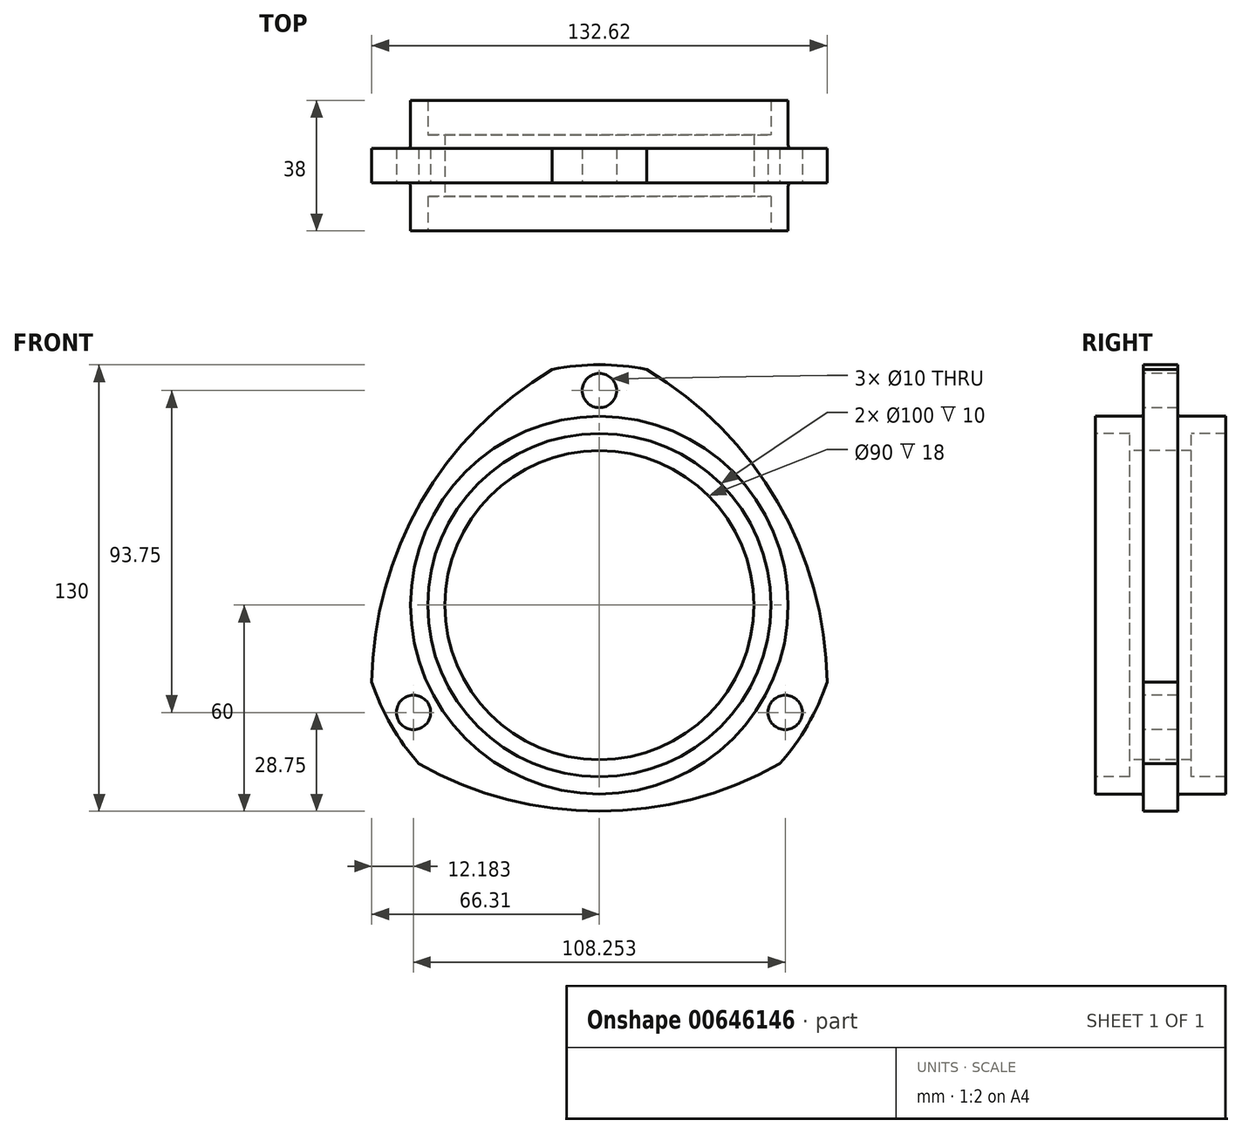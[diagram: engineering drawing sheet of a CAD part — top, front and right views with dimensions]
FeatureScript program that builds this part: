
annotation { "Feature Type Name" : "Feature", "Feature Type Description" : "" }
export const myFeature = defineFeature(function(context is Context, id is Id, definition is map)
    precondition{}
    {
        {
            var Q0;
            Q0=qCreatedBy(makeId("Right.planeOp"),FACE);
            var sketch = newSketch(context, id + "F0", { "sketchPlane" : qUnion([Q0])});
            skLineSegment(sketch, "E0", {"start": v(-36.67, 0) * mm, "end": v(37.6, 0) * mm, "construction": true});
            skLineSegment(sketch, "E1", {"start": v(0, 0) * mm, "end": v(0, 45) * mm, "construction": true});
            skLineSegment(sketch, "E2", {"start": v(-19, 50) * mm, "end": v(-9, 50) * mm});
            skLineSegment(sketch, "E3", {"start": v(-9, 50) * mm, "end": v(-9, 45) * mm});
            skLineSegment(sketch, "E4", {"start": v(-9, 45) * mm, "end": v(9, 45) * mm});
            skLineSegment(sketch, "E5", {"start": v(9, 45) * mm, "end": v(9, 50) * mm});
            skLineSegment(sketch, "E6", {"start": v(9, 50) * mm, "end": v(19, 50) * mm});
            skLineSegment(sketch, "E7", {"start": v(-19, 50) * mm, "end": v(-19, 55) * mm});
            skLineSegment(sketch, "E8", {"start": v(-19, 55) * mm, "end": v(-5, 55) * mm});
            skLineSegment(sketch, "E9", {"start": v(-5, 55) * mm, "end": v(-5, 70) * mm});
            skLineSegment(sketch, "E10", {"start": v(-5, 70) * mm, "end": v(5, 70) * mm});
            skLineSegment(sketch, "E11", {"start": v(5, 70) * mm, "end": v(5, 55) * mm});
            skLineSegment(sketch, "E12", {"start": v(5, 55) * mm, "end": v(19, 55) * mm});
            skLineSegment(sketch, "E13", {"start": v(19, 55) * mm, "end": v(19, 50) * mm});
            skLineSegment(sketch, "E14", {"start": v(0, 70) * mm, "end": v(0, 45) * mm, "construction": true});
            skSolve(sketch);
        }
        {
            var Q0;
            Q0=makeQuery(id+"F0.imprint","IMPRINT",FACE,{"disambiguationData":[TD([[makeQuery(id+"F0.imprint","IMPRINT",EDGE,{"derivedFrom":sQuery(id+"F0.wireOp",EDGE,"E2")}),1.0]])]});
            var Q1;
            Q1=sQuery(id+"F0.wireOp",EDGE,"E0");
            revolve(context, id + "F1", {"entities" : qUnion([Q0]), "axis" : qUnion([Q1]), "revolveType" : RevolveType.FULL});
        }
        {
            var Q0;
            Q0=makeQuery(id+"F1.opRevolve","SWEPT_FACE",FACE,{"disambiguationData":[OSD([sQuery(id+"F0.wireOp",EDGE,"E9")])]});
            var sketch = newSketch(context, id + "F2", { "sketchPlane" : qUnion([Q0])});
            skCircle(sketch, "E15", {"center": v(0, 0) * mm, "radius": 62.5 * mm, "construction": true});
            skCircle(sketch, "E16", {"center": v(0, 62.5) * mm, "radius": 5 * mm});
            skCircle(sketch, "E17.1.0", {"center": v(-54.13, -31.25) * mm, "radius": 5 * mm});
            skCircle(sketch, "E17.2.0", {"center": v(54.13, -31.25) * mm, "radius": 5 * mm});
            skSolve(sketch);
        }
        {
            var Q0;
            Q0 = qSketchRegion(id + "F2", true);
            extrude(context, id + "F3", {"entities" : qUnion([Q0]), "operationType" : NewBodyOperationType.REMOVE, "endBound" : BoundingType.THROUGH_ALL, "oppositeDirection" : true, "depth" : 25 * mm, "offsetDistance" : 25 * mm});
        }
        {
            var Q0;
            Q0=makeQuery(id+"F1.opRevolve","SWEPT_FACE",FACE,{"disambiguationData":[OSD([sQuery(id+"F0.wireOp",EDGE,"E9")])]});
            var sketch = newSketch(context, id + "F4", { "sketchPlane" : qUnion([Q0])});
            skArc(sketch, "E18", {"start": v(13.74, 68.64) * mm, "mid": v(0, 70) * mm, "end": v(-13.74, 68.64) * mm});
            skLineSegment(sketch, "E19", {"start": v(0, 62.5) * mm, "end": v(0, 0) * mm, "construction": true});
            skArc(sketch, "E20.1.0", {"start": v(-66.31, -22.42) * mm, "mid": v(-60.62, -35) * mm, "end": v(-52.57, -46.22) * mm});
            skArc(sketch, "E20.2.0", {"start": v(52.57, -46.22) * mm, "mid": v(60.62, -35) * mm, "end": v(66.31, -22.42) * mm});
            skCircle(sketch, "E21", {"center": v(0, 0) * mm, "radius": 60 * mm, "construction": true});
            skArc(sketch, "E22", {"start": v(66.31, -22.42) * mm, "mid": v(51.96, 30) * mm, "end": v(13.74, 68.64) * mm});
            skArc(sketch, "E23.1.0", {"start": v(-13.74, 68.64) * mm, "mid": v(-51.96, 30) * mm, "end": v(-66.31, -22.42) * mm});
            skArc(sketch, "E23.2.0", {"start": v(-52.57, -46.22) * mm, "mid": v(0, -60) * mm, "end": v(52.57, -46.22) * mm});
            skCircle(sketch, "E24", {"center": v(0, 0) * mm, "radius": 81.96 * mm});
            skSolve(sketch);
        }
        {
            var Q0;
            Q0 = qSketchRegion(id + "F4", true);
            extrude(context, id + "F5", {"entities" : qUnion([Q0]), "operationType" : NewBodyOperationType.REMOVE, "endBound" : BoundingType.THROUGH_ALL, "oppositeDirection" : true, "depth" : 25 * mm, "offsetDistance" : 25 * mm});
        }
        {
            var Q0;
            Q0=makeQuery(id+"F1.opRevolve","SWEPT_EDGE",EDGE,{"disambiguationData":[OSD([sQuery(id+"F0.wireOp",EDGE,"E8"),sQuery(id+"F0.wireOp",EDGE,"E9")])]});
            var Q1;
            Q1=makeQuery(id+"F1.opRevolve","SWEPT_EDGE",EDGE,{"disambiguationData":[OSD([sQuery(id+"F0.wireOp",EDGE,"E11"),sQuery(id+"F0.wireOp",EDGE,"E12")])]});
            fillet(context, id + "F6", {"entities" : qUnion([Q0, Q1]), "radius" : 1 * mm, "tangentPropagation" : true, "allowEdgeOverflow" : false});
        }
    });
